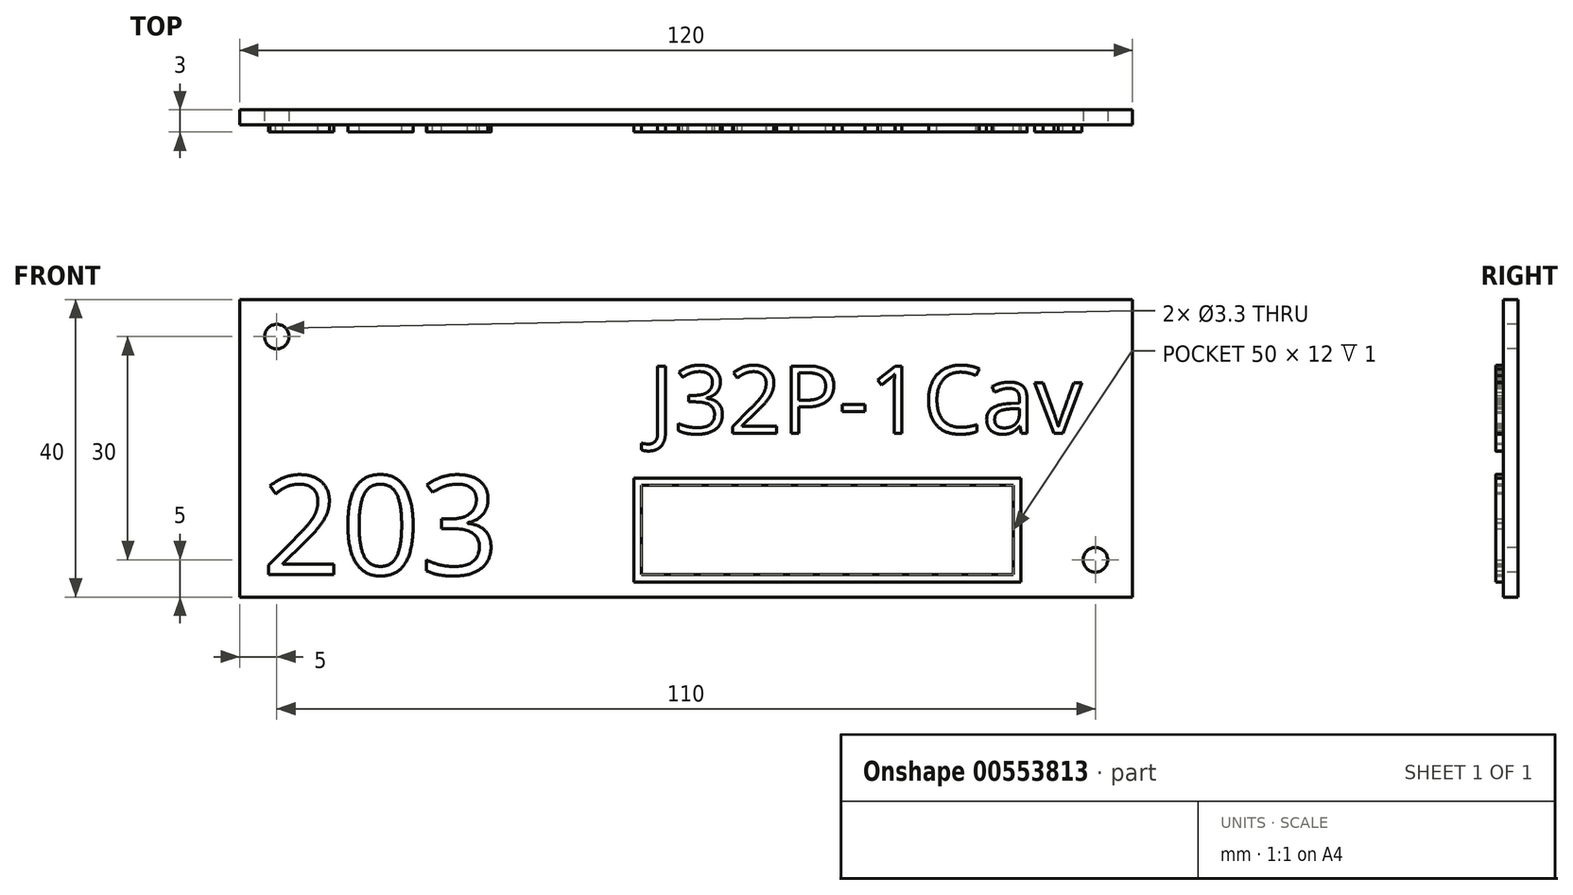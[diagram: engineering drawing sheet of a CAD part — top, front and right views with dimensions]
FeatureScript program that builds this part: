
annotation { "Feature Type Name" : "Feature", "Feature Type Description" : "" }
export const myFeature = defineFeature(function(context is Context, id is Id, definition is map)
    precondition{}
    {
        {
            var Q0;
            Q0=qCreatedBy(makeId("Front.planeOp"),FACE);
            var sketch = newSketch(context, id + "F0", { "sketchPlane" : qUnion([Q0])});
            skLineSegment(sketch, "E0.bottom", {"start": v(60, -20) * mm, "end": v(-60, -20) * mm});
            skLineSegment(sketch, "E0.top", {"start": v(60, 20) * mm, "end": v(-60, 20) * mm});
            skLineSegment(sketch, "E0.left", {"start": v(60, -20) * mm, "end": v(60, 20) * mm});
            skLineSegment(sketch, "E0.right", {"start": v(-60, -20) * mm, "end": v(-60, 20) * mm});
            skPoint(sketch, "E0.middle", {"position": v(0, 0) * mm});
            skSolve(sketch);
        }
        {
            var Q0;
            Q0=makeQuery(id+"F0.imprint","IMPRINT",FACE,{"disambiguationData":[TD([[makeQuery(id+"F0.imprint","IMPRINT",EDGE,{"derivedFrom":sQuery(id+"F0.wireOp",EDGE,"E0.bottom")}),-1.0]])]});
            extrude(context, id + "F1", {"entities" : qUnion([Q0]), "depth" : 2 * mm});
        }
        {
            var Q0;
            Q0=makeQuery(id+"F1.opExtrude","CAP_FACE",FACE,{"disambiguationData":[OSD([sQuery(id+"F0.wireOp",EDGE,"E0.bottom"),sQuery(id+"F0.wireOp",EDGE,"E0.top"),sQuery(id+"F0.wireOp",EDGE,"E0.left"),sQuery(id+"F0.wireOp",EDGE,"E0.right")])],"isStart":false});
            var sketch = newSketch(context, id + "F2", { "sketchPlane" : qUnion([Q0])});
            skPoint(sketch, "E1", {"position": v(-55, 15) * mm});
            skPoint(sketch, "E2", {"position": v(55, -15) * mm});
            skSolve(sketch);
        }
        {
            var Q0;
            Q0=sQuery(id+"F2.wireOp",VERTEX,"E1");
            var Q1;
            Q1=sQuery(id+"F2.wireOp",VERTEX,"E2");
            var Q2;
            Q2=makeQuery(id+"F1.opExtrude","SWEPT_BODY",BODY,{"disambiguationData":[OSD([sQuery(id+"F0.wireOp",EDGE,"E0.bottom"),sQuery(id+"F0.wireOp",EDGE,"E0.top"),sQuery(id+"F0.wireOp",EDGE,"E0.left"),sQuery(id+"F0.wireOp",EDGE,"E0.right")])]});
            hole(context, id + "F3", {"style" : HoleStyle.SIMPLE, "endStyle" : HoleEndStyle.THROUGH, "holeDiameter" : 3.3 * mm, "locations" : qUnion([Q0, Q1]), "scope" : qUnion([Q2]), "isTappedThrough" : true});
        }
        {
            var Q0;
            Q0=makeQuery(id+"F1.opExtrude","CAP_FACE",FACE,{"disambiguationData":[OSD([sQuery(id+"F0.wireOp",EDGE,"E0.bottom"),sQuery(id+"F0.wireOp",EDGE,"E0.top"),sQuery(id+"F0.wireOp",EDGE,"E0.left"),sQuery(id+"F0.wireOp",EDGE,"E0.right")])],"isStart":false});
            var sketch = newSketch(context, id + "F4", { "sketchPlane" : qUnion([Q0])});
            skText(sketch, "E3", { "text": "J32P-1Cav", "fontName": "OpenSans-Regular.ttf"});
            const initialGuessF4  = {"E3": [-0.005, 0.002, 1, 0, 0.00912]};
            skSetInitialGuess(sketch, initialGuessF4);
            skSolve(sketch);
        }
        {
            var Q0;
            Q0=qSketchRegion(id+"F4",true);
            extrude(context, id + "F5", {"entities" : qUnion([Q0]), "operationType" : NewBodyOperationType.ADD, "depth" : 1 * mm});
        }
        {
            var Q0;
            {var subQ0=sQuery(id+"F0.wireOp",EDGE,"E0.top");var subQ1=sQuery(id+"F0.wireOp",EDGE,"E0.left");var subQ2=sQuery(id+"F0.wireOp",EDGE,"E0.right");var subQ3=sQuery(id+"F0.wireOp",EDGE,"E0.bottom");Q0=makeQuery(id+"F5.boolean.opBoolean","SPLIT",FACE,{"disambiguationData":[TD([makeQuery(id+"F1.opExtrude","SWEPT_FACE",FACE,{"disambiguationData":[OSD([subQ3])]})])],"derivedFrom":makeQuery(id+"F1.opExtrude","CAP_FACE",FACE,{"disambiguationData":[OSD([subQ3,subQ0,subQ1,subQ2])],"isStart":false})});}
            var sketch = newSketch(context, id + "F6", { "sketchPlane" : qUnion([Q0])});
            skText(sketch, "E4", { "text": "203", "fontName": "OpenSans-Regular.ttf"});
            const initialGuessF6  = {"E4": [-0.057, -0.017, 1, 0, 0.01338]};
            skSetInitialGuess(sketch, initialGuessF6);
            skSolve(sketch);
        }
        {
            var Q0;
            Q0=qSketchRegion(id+"F6",true);
            extrude(context, id + "F7", {"entities" : qUnion([Q0]), "operationType" : NewBodyOperationType.ADD, "depth" : 1 * mm});
        }
        {
            var Q0;
            {var subQ46=sQuery(id+"F0.wireOp",EDGE,"E0.top");var subQ48=sQuery(id+"F0.wireOp",EDGE,"E0.left");var subQ66=sQuery(id+"F0.wireOp",EDGE,"E0.right");var subQ76=sQuery(id+"F0.wireOp",EDGE,"E0.bottom");var subQ77=makeQuery(id+"F1.opExtrude","SWEPT_FACE",FACE,{"disambiguationData":[OSD([subQ76])]});Q0=makeQuery(id+"F7.boolean.opBoolean","SPLIT",FACE,{"disambiguationData":[TD([subQ77])],"derivedFrom":makeQuery(id+"F5.boolean.opBoolean","SPLIT",FACE,{"disambiguationData":[TD([subQ77])],"derivedFrom":makeQuery(id+"F1.opExtrude","CAP_FACE",FACE,{"disambiguationData":[OSD([subQ76,subQ46,subQ48,subQ66])],"isStart":false})})});}
            var sketch = newSketch(context, id + "F8", { "sketchPlane" : qUnion([Q0])});
            skLineSegment(sketch, "E5.bottom", {"start": v(45, -18) * mm, "end": v(-7, -18) * mm});
            skLineSegment(sketch, "E5.top", {"start": v(45, -4) * mm, "end": v(-7, -4) * mm});
            skLineSegment(sketch, "E5.left", {"start": v(45, -18) * mm, "end": v(45, -4) * mm});
            skLineSegment(sketch, "E5.right", {"start": v(-7, -18) * mm, "end": v(-7, -4) * mm});
            skPoint(sketch, "E5.middle", {"position": v(19, -11) * mm});
            skLineSegment(sketch, "E6.0", {"start": v(44, -5) * mm, "end": v(-6, -5) * mm});
            skLineSegment(sketch, "E6.1", {"start": v(44, -17) * mm, "end": v(44, -5) * mm});
            skLineSegment(sketch, "E6.2", {"start": v(44, -17) * mm, "end": v(-6, -17) * mm});
            skLineSegment(sketch, "E6.3", {"start": v(-6, -17) * mm, "end": v(-6, -5) * mm});
            skSolve(sketch);
        }
        {
            var Q0;
            Q0=makeQuery(id+"F8.imprint","IMPRINT",FACE,{"disambiguationData":[TD([[makeQuery(id+"F8.imprint","IMPRINT",EDGE,{"derivedFrom":sQuery(id+"F8.wireOp",EDGE,"E5.bottom")}),-1.0]])]});
            extrude(context, id + "F9", {"entities" : qUnion([Q0]), "operationType" : NewBodyOperationType.ADD, "depth" : 1 * mm});
        }
    });
